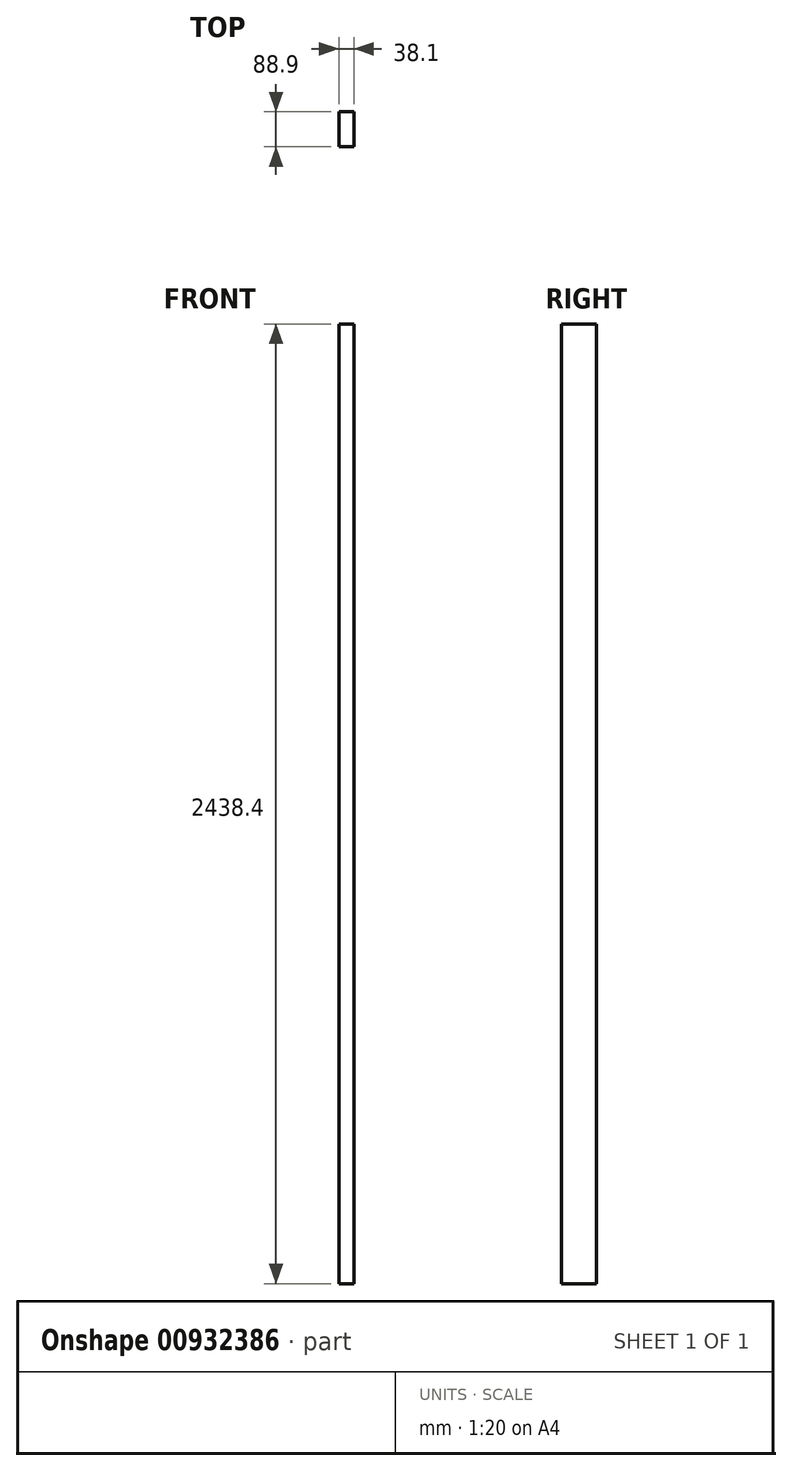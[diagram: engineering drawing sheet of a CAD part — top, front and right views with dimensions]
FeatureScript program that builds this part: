
annotation { "Feature Type Name" : "Feature", "Feature Type Description" : "" }
export const myFeature = defineFeature(function(context is Context, id is Id, definition is map)
    precondition{}
    {
        {
            var Q0;
            Q0=qCreatedBy(makeId("Top.planeOp"),FACE);
            var sketch = newSketch(context, id + "F0", { "sketchPlane" : qUnion([Q0])});
            skLineSegment(sketch, "E0.bottom", {"start": v(-19.05, 44.45) * mm, "end": v(19.05, 44.45) * mm});
            skLineSegment(sketch, "E0.top", {"start": v(-19.05, -44.45) * mm, "end": v(19.05, -44.45) * mm});
            skLineSegment(sketch, "E0.left", {"start": v(-19.05, 44.45) * mm, "end": v(-19.05, -44.45) * mm});
            skLineSegment(sketch, "E0.right", {"start": v(19.05, 44.45) * mm, "end": v(19.05, -44.45) * mm});
            skPoint(sketch, "E0.middle", {"position": v(0, 0) * mm});
            skSolve(sketch);
        }
        {
            var Q0;
            Q0=makeQuery(id+"F0.imprint","IMPRINT",FACE,{"disambiguationData":[TD([[makeQuery(id+"F0.imprint","IMPRINT",EDGE,{"derivedFrom":sQuery(id+"F0.wireOp",EDGE,"E0.bottom")}),-1.0]])]});
            extrude(context, id + "F1", {"entities" : qUnion([Q0]), "depth" : 2438.4 * mm, "offsetDistance" : 25.4 * mm});
        }
    });
